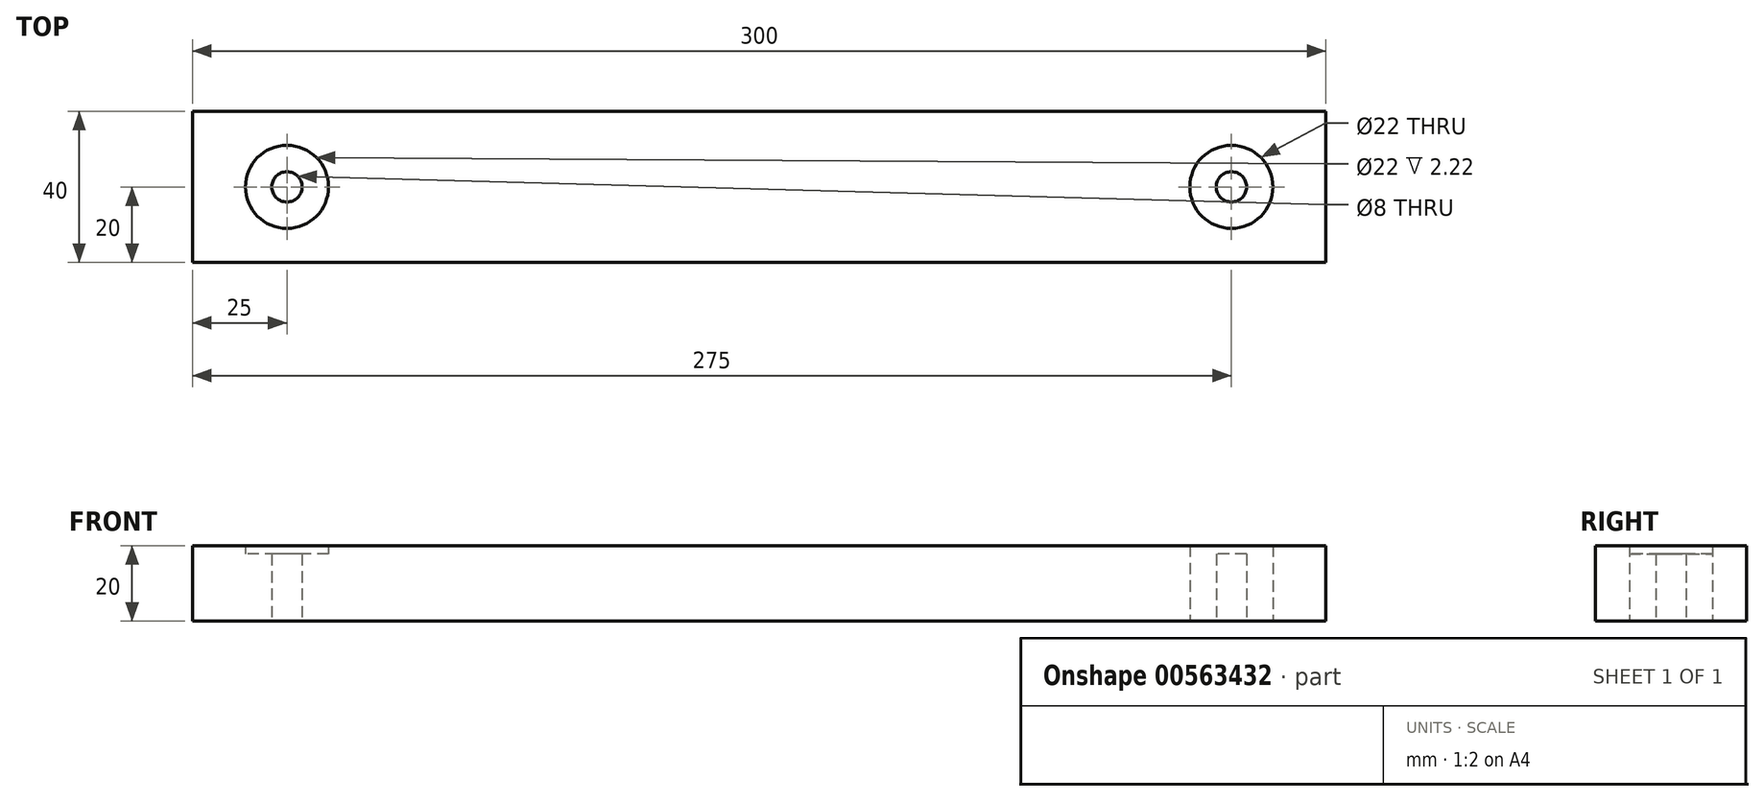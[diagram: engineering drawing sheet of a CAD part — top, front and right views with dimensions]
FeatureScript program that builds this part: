
annotation { "Feature Type Name" : "Feature", "Feature Type Description" : "" }
export const myFeature = defineFeature(function(context is Context, id is Id, definition is map)
    precondition{}
    {
        {
            var Q0;
            Q0=qCreatedBy(makeId("Top.planeOp"),FACE);
            var sketch = newSketch(context, id + "F0", { "sketchPlane" : qUnion([Q0])});
            skLineSegment(sketch, "E0.bottom", {"start": v(150, 20) * mm, "end": v(-150, 20) * mm});
            skLineSegment(sketch, "E0.top", {"start": v(150, -20) * mm, "end": v(-150, -20) * mm});
            skLineSegment(sketch, "E0.left", {"start": v(150, 20) * mm, "end": v(150, -20) * mm});
            skLineSegment(sketch, "E0.right", {"start": v(-150, 20) * mm, "end": v(-150, -20) * mm});
            skPoint(sketch, "E0.middle", {"position": v(0, 0) * mm});
            skPoint(sketch, "E1", {"position": v(-125, 20) * mm});
            skPoint(sketch, "E2", {"position": v(-125, -20) * mm});
            skLineSegment(sketch, "E3", {"start": v(-150, 20) * mm, "end": v(-125, 20) * mm});
            skPoint(sketch, "E4", {"position": v(125, 20) * mm});
            skPoint(sketch, "E5", {"position": v(125, -20) * mm});
            skLineSegment(sketch, "E6", {"start": v(125, 20) * mm, "end": v(150, 20) * mm});
            skLineSegment(sketch, "E7", {"start": v(-150, 0) * mm, "end": v(150, 0) * mm});
            skPoint(sketch, "E8", {"position": v(-125, 0) * mm});
            skPoint(sketch, "E9", {"position": v(125, 0) * mm});
            skCircle(sketch, "E10", {"center": v(-125, 0) * mm, "radius": 11 * mm});
            skCircle(sketch, "E11", {"center": v(125, 0) * mm, "radius": 11 * mm});
            skCircle(sketch, "E12", {"center": v(-125, 0) * mm, "radius": 4 * mm});
            skCircle(sketch, "E13", {"center": v(125, 0) * mm, "radius": 4 * mm});
            skSolve(sketch);
        }
        {
            var Q0;
            {var subQ1=sQuery(id+"F0.wireOp",EDGE,"E0.top");Q0=makeQuery(id+"F0.imprint","IMPRINT",FACE,{"disambiguationData":[TD([[makeQuery(id+"F0.imprint","IMPRINT",EDGE,{"derivedFrom":subQ1}),-1.0]])]});}
            var Q1;
            Q1=makeQuery(id+"F0.imprint","IMPRINT",FACE,{"disambiguationData":[TD([[makeQuery(id+"F0.imprint","IMPRINT",EDGE,{"derivedFrom":sQuery(id+"F0.wireOp",EDGE,"E0.bottom")}),1.0]])]});
            extrude(context, id + "F1", {"entities" : qUnion([Q0, Q1]), "depth" : 20 * mm, "offsetDistance" : 25.4 * mm});
        }
        {
            var Q0;
            Q0 = qSketchRegion(id + "F0", true);
            var Q1;
            {var subQ0=sQuery(id+"F0.wireOp",EDGE,"E12");var subQ1=sQuery(id+"F0.wireOp",EDGE,"E7");var subQ2=makeQuery(id+"F0.imprint","INTERSECT",VERTEX,{"disambiguationData":[OD(0.0)],"derivedFrom":[subQ1,subQ0]});Q1=makeQuery(id+"F0.imprint","IMPRINT",FACE,{"disambiguationData":[TD([[makeQuery(id+"F0.imprint","IMPRINT",EDGE,{"disambiguationData":[TD([[subQ2,-1.0]])],"derivedFrom":subQ1}),-1.0]])]});}
            var Q2;
            {var subQ0=sQuery(id+"F0.wireOp",EDGE,"E12");var subQ1=sQuery(id+"F0.wireOp",EDGE,"E7");var subQ2=makeQuery(id+"F0.imprint","INTERSECT",VERTEX,{"disambiguationData":[OD(0.0)],"derivedFrom":[subQ1,subQ0]});Q2=makeQuery(id+"F0.imprint","IMPRINT",FACE,{"disambiguationData":[TD([[makeQuery(id+"F0.imprint","IMPRINT",EDGE,{"disambiguationData":[TD([[subQ2,-1.0]])],"derivedFrom":subQ1}),1.0]])]});}
            var Q3;
            {var subQ0=sQuery(id+"F0.wireOp",EDGE,"E13");var subQ1=sQuery(id+"F0.wireOp",EDGE,"E7");var subQ2=makeQuery(id+"F0.imprint","INTERSECT",VERTEX,{"disambiguationData":[OD(0.0)],"derivedFrom":[subQ1,subQ0]});Q3=makeQuery(id+"F0.imprint","IMPRINT",FACE,{"disambiguationData":[TD([[makeQuery(id+"F0.imprint","IMPRINT",EDGE,{"disambiguationData":[TD([[subQ2,-1.0]])],"derivedFrom":subQ1}),1.0]])]});}
            var Q4;
            {var subQ0=sQuery(id+"F0.wireOp",EDGE,"E13");var subQ1=sQuery(id+"F0.wireOp",EDGE,"E7");var subQ2=makeQuery(id+"F0.imprint","INTERSECT",VERTEX,{"disambiguationData":[OD(0.0)],"derivedFrom":[subQ1,subQ0]});Q4=makeQuery(id+"F0.imprint","IMPRINT",FACE,{"disambiguationData":[TD([[makeQuery(id+"F0.imprint","IMPRINT",EDGE,{"disambiguationData":[TD([[subQ2,-1.0]])],"derivedFrom":subQ1}),-1.0]])]});}
            extrude(context, id + "F2", {"entities" : qUnion([Q0, Q1, Q2, Q3, Q4]), "operationType" : NewBodyOperationType.ADD, "depth" : 17.78 * mm, "offsetDistance" : 25.4 * mm});
        }
    });
